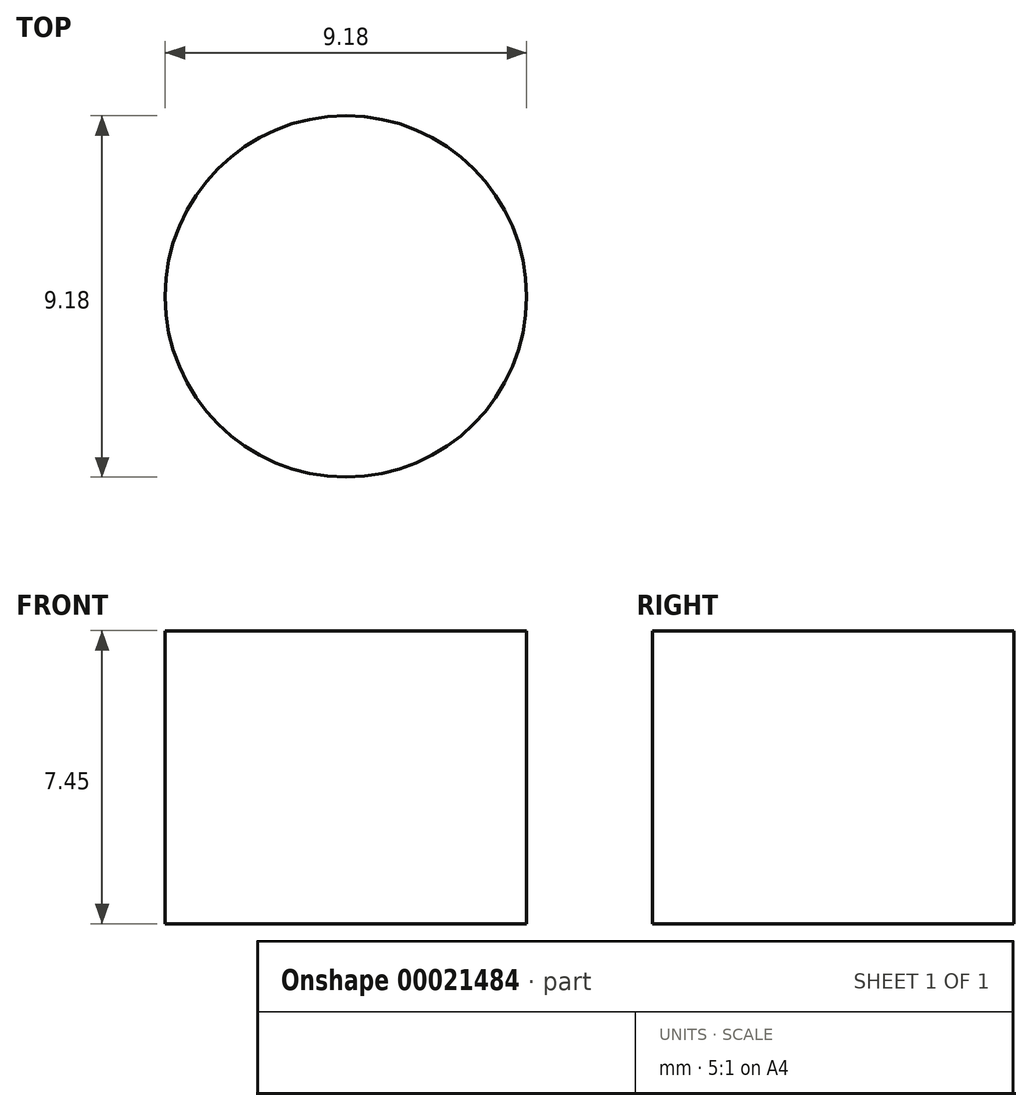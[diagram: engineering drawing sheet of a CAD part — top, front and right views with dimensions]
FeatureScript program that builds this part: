
annotation { "Feature Type Name" : "Feature", "Feature Type Description" : "" }
export const myFeature = defineFeature(function(context is Context, id is Id, definition is map)
    precondition{}
    {
        {
            var Q0;
            Q0=qCreatedBy(makeId("Top.planeOp"),FACE);
            var sketch = newSketch(context, id + "F0", { "sketchPlane" : qUnion([Q0])});
            skLineSegment(sketch, "E0", {"start": v(0, 0) * mm, "end": v(0, 50.68) * mm});
            skCircle(sketch, "E1", {"center": v(0, 50.68) * mm, "radius": 10.54 * mm});
            skCircle(sketch, "E2", {"center": v(0, 0) * mm, "radius": 4.6 * mm});
            skLineSegment(sketch, "E3", {"start": v(10.54, 50.5) * mm, "end": v(4.62, 0) * mm});
            skLineSegment(sketch, "E4", {"start": v(-10.52, 50.02) * mm, "end": v(-4.62, 0) * mm});
            skSolve(sketch);
        }
        {
            var Q0;
            {var subQ1=sQuery(id+"F0.wireOp",EDGE,"E1");var subQ7=makeQuery(id+"F0.imprint","IMPRINT",VERTEX,{"derivedFrom":subQ1});Q0=makeQuery(id+"F0.imprint","IMPRINT",FACE,{"disambiguationData":[TD([[makeQuery(id+"F0.imprint","IMPRINT",EDGE,{"disambiguationData":[TD([[subQ7,1.0]])],"derivedFrom":subQ1}),1.0]])]});}
            var Q1;
            Q1=makeQuery(id+"F0.imprint","IMPRINT",FACE,{"disambiguationData":[TD([[makeQuery(id+"F0.imprint","IMPRINT",EDGE,{"derivedFrom":sQuery(id+"F0.wireOp",EDGE,"E2")}),1.0]])]});
            extrude(context, id + "F1", {"entities" : qUnion([Q0, Q1]), "depth" : 7.45 * mm});
        }
    });
